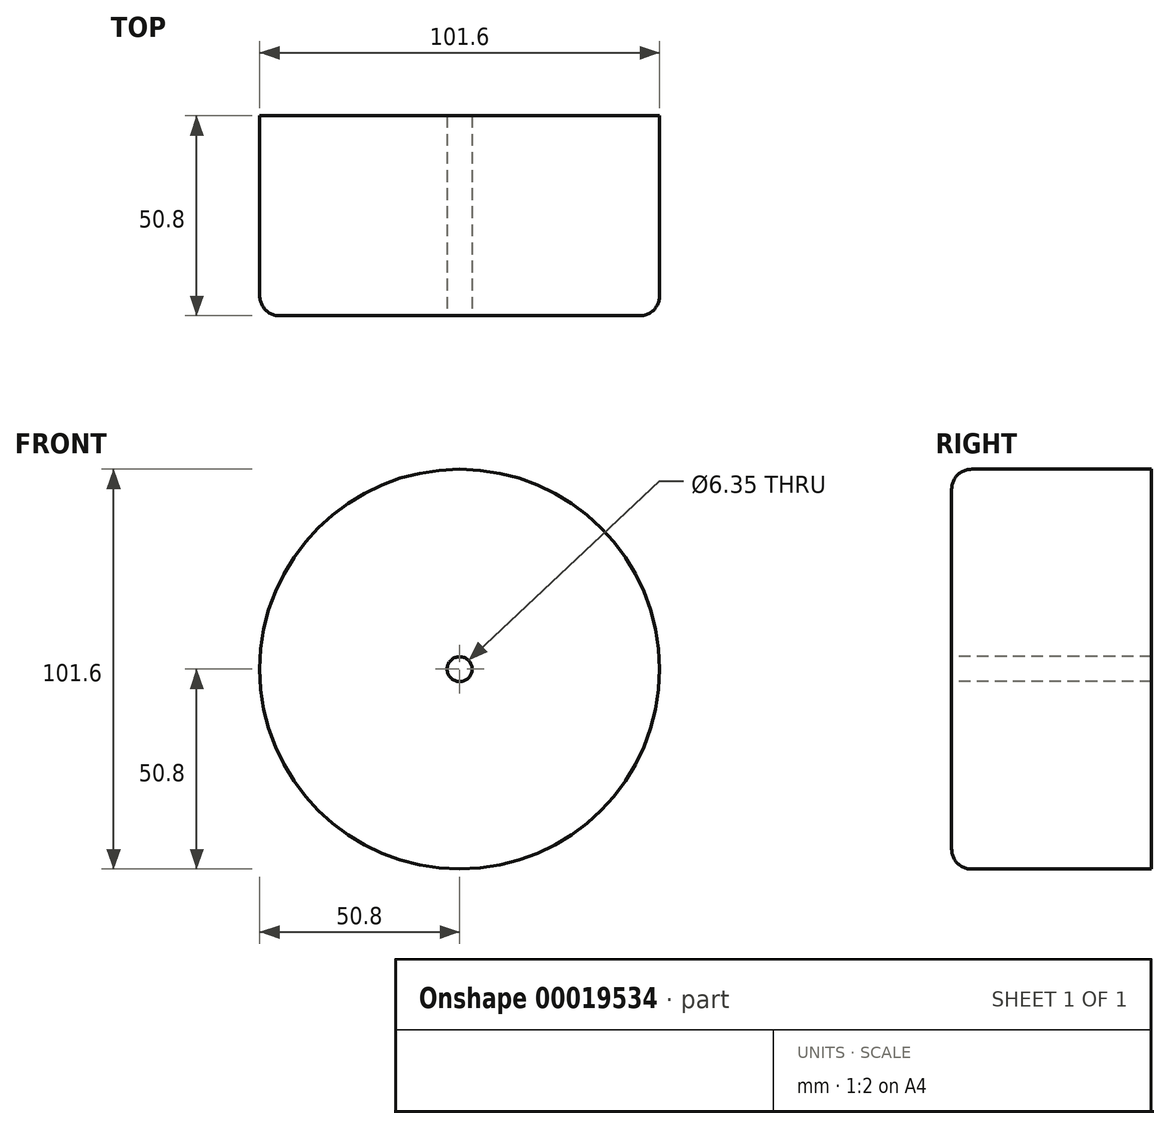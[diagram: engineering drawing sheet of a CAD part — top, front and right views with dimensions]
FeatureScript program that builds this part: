
annotation { "Feature Type Name" : "Feature", "Feature Type Description" : "" }
export const myFeature = defineFeature(function(context is Context, id is Id, definition is map)
    precondition{}
    {
        {
            var Q0;
            Q0=qCreatedBy(makeId("Front.planeOp"),FACE);
            var sketch = newSketch(context, id + "F0", { "sketchPlane" : qUnion([Q0])});
            skCircle(sketch, "E0", {"center": v(0, 0) * mm, "radius": 50.8 * mm});
            skSolve(sketch);
        }
        {
            var Q0;
            Q0=makeQuery(id+"F0.imprint","IMPRINT",FACE,{"disambiguationData":[TD([[makeQuery(id+"F0.imprint","IMPRINT",EDGE,{"derivedFrom":sQuery(id+"F0.wireOp",EDGE,"E0")}),1.0]])]});
            extrude(context, id + "F1", {"entities" : qUnion([Q0]), "endBound" : BoundingType.SYMMETRIC, "depth" : 50.8 * mm});
        }
        {
            var Q0;
            Q0=makeQuery(id+"F1.opExtrude","CAP_EDGE",EDGE,{"disambiguationData":[OSD([sQuery(id+"F0.wireOp",EDGE,"E0")])],"isStart":false});
            fillet(context, id + "F2", {"entities" : qUnion([Q0]), "radius" : 5.08 * mm, "tangentPropagation" : true, "allowEdgeOverflow" : false});
        }
        {
            var Q0;
            Q0=makeQuery(id+"F1.opExtrude","CAP_FACE",FACE,{"disambiguationData":[OSD([sQuery(id+"F0.wireOp",EDGE,"E0")])],"isStart":false});
            var sketch = newSketch(context, id + "F3", { "sketchPlane" : qUnion([Q0])});
            skCircle(sketch, "E1", {"center": v(0, 0) * mm, "radius": 3.18 * mm});
            skSolve(sketch);
        }
        {
            var Q0;
            Q0=makeQuery(id+"F3.imprint","IMPRINT",FACE,{"disambiguationData":[TD([[makeQuery(id+"F3.imprint","IMPRINT",EDGE,{"derivedFrom":sQuery(id+"F3.wireOp",EDGE,"E1")}),1.0]])]});
            extrude(context, id + "F4", {"entities" : qUnion([Q0]), "operationType" : NewBodyOperationType.REMOVE, "endBound" : BoundingType.UP_TO_NEXT, "oppositeDirection" : true, "depth" : 25.4 * mm});
        }
    });
